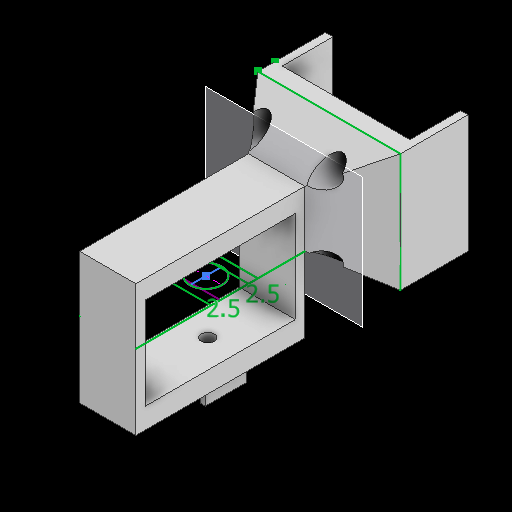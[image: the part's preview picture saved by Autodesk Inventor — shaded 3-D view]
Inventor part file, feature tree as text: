
AUTODESK INVENTOR PART (.ipt)
format: ipt  version: 2025.1 (Build 291241000, 241)  size: 344,576 bytes
history: native  units: in
note: dims shown in document units (in); Inventor stores cm internally (conversion verified against a paired STEP export)
features: sketch x29, extrude x19, projected_geometry x12, other x6, loft x1
ambient origin geometry x8: Origin, YZ Plane, XZ Plane, XY Plane, X Axis, Y Axis, Z Axis, Center Point
bodies: Body1 (feature_tree)
feature tree (67):
  other  "솔리드1"
  extrude  "돌출1"  Depth=1.4961in
  extrude  "돌출2"  Depth=1.2402in
  sketch  "스케치3"
  other  "작업 평면1"
  sketch  "스케치4"
  loft  "로프트1"
  extrude  "돌출3"  Depth=0.0787in
  sketch  "스케치7"
  other  "작업 평면2"
  sketch  "스케치8"
  sketch  "스케치9"
  sketch  "스케치10"
  extrude  "돌출4"  Depth=0.0787in
  extrude  "돌출5"  Depth=0.5315in TaperAngle=0.0deg
  extrude  "돌출6"  Depth=0.4724in
  extrude  "돌출7"  Depth=0.6693in
  extrude  "돌출8"  Depth=0.6201in
  sketch  "스케치14"
  sketch  "스케치15"
  extrude  "돌출10"  Depth=0.5906in
  sketch  "스케치17"
  sketch  "스케치18"
  sketch  "스케치19"
  extrude  "돌출11"  Depth=0.5906in
  extrude  "돌출12"  Depth=0.2953in
  extrude  "돌출13"  Depth=0.2953in
  sketch  "스케치22"
  extrude  "돌출14"  TaperAngle=0.0deg  [1 undecoded]
  extrude  "돌출15"  TaperAngle=0.0deg  [1 undecoded]
  extrude  "돌출16"  Depth=0.1575in
  extrude  "돌출17"  Depth=0.1969in
  sketch  "스케치27"
  extrude  "돌출18"  Depth=0.2165in
  extrude  "돌출19"  Depth=0.7874in
  extrude  "돌출20"  Depth=0.7874in
  sketch  "스케치1"
  sketch  "스케치2"
  projected_geometry  "투영된 루프1"
  projected_geometry  "투영된 루프2"
  sketch  "스케치5"
  other  "모서리1"
  sketch  "스케치6"
  projected_geometry  "투영된 루프3"
  other  "스케치 - 직사각형 패턴1"
  other  "스케치 - 직사각형 패턴2"
  sketch  "스케치11"
  sketch  "스케치12"
  projected_geometry  "투영된 루프4"
  projected_geometry  "투영된 루프5"
  projected_geometry  "투영된 루프6"
  sketch  "스케치16"
  projected_geometry  "투영된 루프7"
  projected_geometry  "투영된 루프8"
  sketch  "스케치20"
  sketch  "스케치21"
  projected_geometry  "투영된 루프9"
  sketch  "스케치23"
  sketch  "스케치24"
  sketch  "스케치25"
  projected_geometry  "투영된 루프10"
  sketch  "스케치26"
  projected_geometry  "투영된 루프11"
  projected_geometry  "투영된 루프12"
  sketch  "스케치28"
  sketch  "스케치29"
  sketch  "스케치30"
note: 2 required parameter values undecoded (feature->parameter linkage not recoverable at this tier; creation-order binding heuristic only, values carry confidence <= 0.55)
